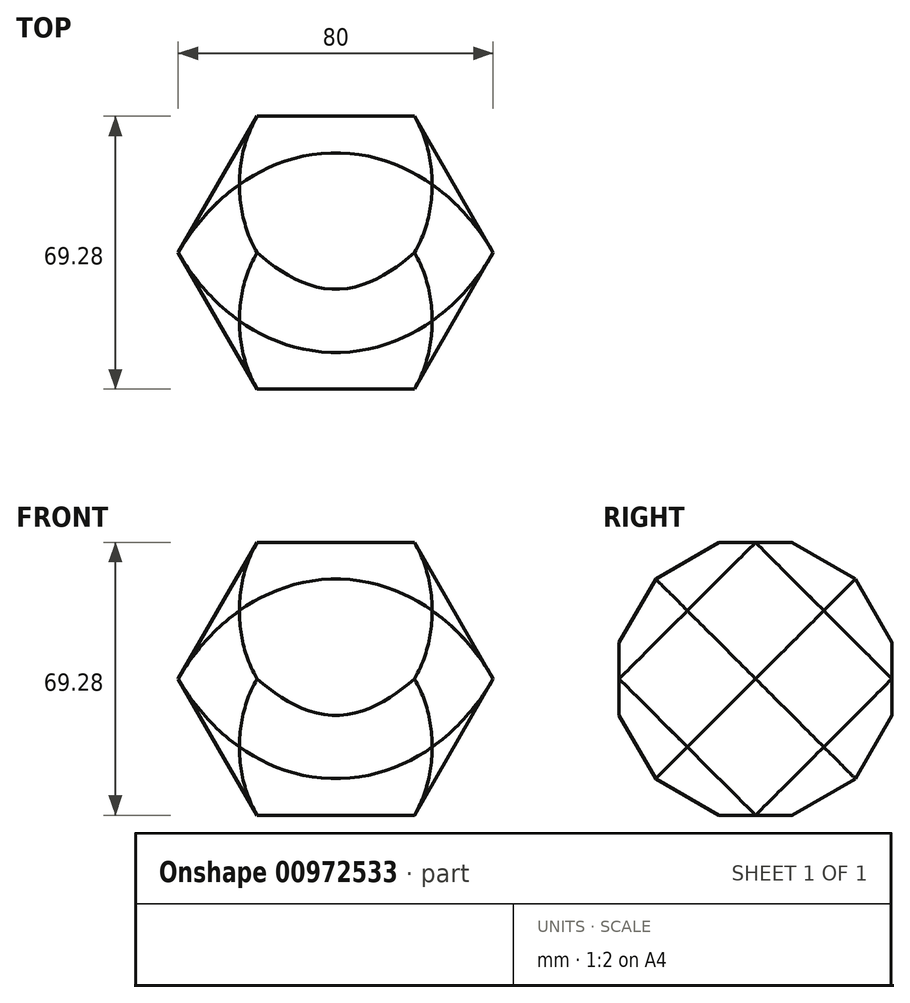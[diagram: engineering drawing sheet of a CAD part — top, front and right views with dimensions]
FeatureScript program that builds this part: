
annotation { "Feature Type Name" : "Feature", "Feature Type Description" : "" }
export const myFeature = defineFeature(function(context is Context, id is Id, definition is map)
    precondition{}
    {
        {
            var Q0;
            Q0=qCreatedBy(makeId("Front.planeOp"),FACE);
            var sketch = newSketch(context, id + "F0", { "sketchPlane" : qUnion([Q0])});
            skCircle(sketch, "E0.cCircle", {"center": v(0, 0) * mm, "radius": 40 * mm, "construction": true});
            skLineSegment(sketch, "E0.0", {"start": v(40, 0) * mm, "end": v(20, -34.64) * mm});
            skLineSegment(sketch, "E0.1", {"start": v(20, -34.64) * mm, "end": v(0, -34.64) * mm});
            skLineSegment(sketch, "E0.4", {"start": v(0, 34.64) * mm, "end": v(20, 34.64) * mm});
            skLineSegment(sketch, "E0.5", {"start": v(20, 34.64) * mm, "end": v(40, 0) * mm});
            skLineSegment(sketch, "E1", {"start": v(0, -34.64) * mm, "end": v(0, 34.64) * mm});
            skPoint(sketch, "E0.2.start.orphan", {"position": v(-20, -34.64) * mm});
            skPoint(sketch, "E2.orphan", {"position": v(-20, 34.64) * mm});
            skSolve(sketch);
        }
        {
            var Q0;
            Q0 = qSketchRegion(id + "F0", true);
            var Q1;
            Q1=sQuery(id+"F0.wireOp",EDGE,"E1");
            revolve(context, id + "F1", {"surfaceOperationType" : NewSurfaceOperationType.NEW, "entities" : qUnion([Q0]), "axis" : qUnion([Q1]), "revolveType" : RevolveType.FULL});
        }
        {
            var Q0;
            Q0=qCreatedBy(makeId("Right.planeOp"),FACE);
            var sketch = newSketch(context, id + "F2", { "sketchPlane" : qUnion([Q0])});
            skCircle(sketch, "E3.cCircle", {"center": v(0, 0) * mm, "radius": 40 * mm, "construction": true});
            skLineSegment(sketch, "E3.0", {"start": v(0, 40) * mm, "end": v(34.64, 20) * mm});
            skLineSegment(sketch, "E3.1", {"start": v(34.64, 20) * mm, "end": v(34.64, 0) * mm});
            skLineSegment(sketch, "E3.4", {"start": v(-34.64, 0) * mm, "end": v(-34.64, 20) * mm});
            skLineSegment(sketch, "E3.5", {"start": v(-34.64, 20) * mm, "end": v(0, 40) * mm});
            skLineSegment(sketch, "E4", {"start": v(34.64, 0) * mm, "end": v(59.27, 0) * mm});
            skPoint(sketch, "E3.3.end.orphan", {"position": v(-34.64, -20) * mm});
            skPoint(sketch, "E5.orphan", {"position": v(34.64, -20) * mm});
            skLineSegment(sketch, "E6.bottom", {"start": v(-42.02, 40) * mm, "end": v(42.02, 40) * mm});
            skLineSegment(sketch, "E6.left", {"start": v(-42.02, 40) * mm, "end": v(-42.02, 0) * mm});
            skLineSegment(sketch, "E6.right", {"start": v(42.02, 40) * mm, "end": v(42.02, 0) * mm});
            skLineSegment(sketch, "E7", {"start": v(-42.02, 0) * mm, "end": v(-34.64, 0) * mm});
            skPoint(sketch, "E8.orphan", {"position": v(42.02, -40) * mm});
            skPoint(sketch, "E6.top.start.orphan", {"position": v(-42.02, -40) * mm});
            skLineSegment(sketch, "E9.trimOffspring", {"start": v(34.64, 0) * mm, "end": v(42.02, 0) * mm});
            skSolve(sketch);
        }
        {
            var Q0;
            {var subQ2=sQuery(id+"F2.wireOp",EDGE,"E3.0");Q0=makeQuery(id+"F2.imprint","IMPRINT",FACE,{"disambiguationData":[TD([[makeQuery(id+"F2.imprint","IMPRINT",EDGE,{"derivedFrom":subQ2}),1.0]])]});}
            var Q1;
            Q1=makeQuery(id+"F2.imprint","IMPRINT",FACE,{"disambiguationData":[TD([[makeQuery(id+"F2.imprint","IMPRINT",EDGE,{"derivedFrom":sQuery(id+"F2.wireOp",EDGE,"E3.4")}),1.0]])]});
            var Q2;
            Q2=sQuery(id+"F2.wireOp",EDGE,"E4");
            revolve(context, id + "F3", {"operationType" : NewBodyOperationType.REMOVE, "surfaceOperationType" : NewSurfaceOperationType.NEW, "entities" : qUnion([Q0, Q1]), "axis" : qUnion([Q2]), "revolveType" : RevolveType.FULL, "oppositeDirection" : true});
        }
    });
